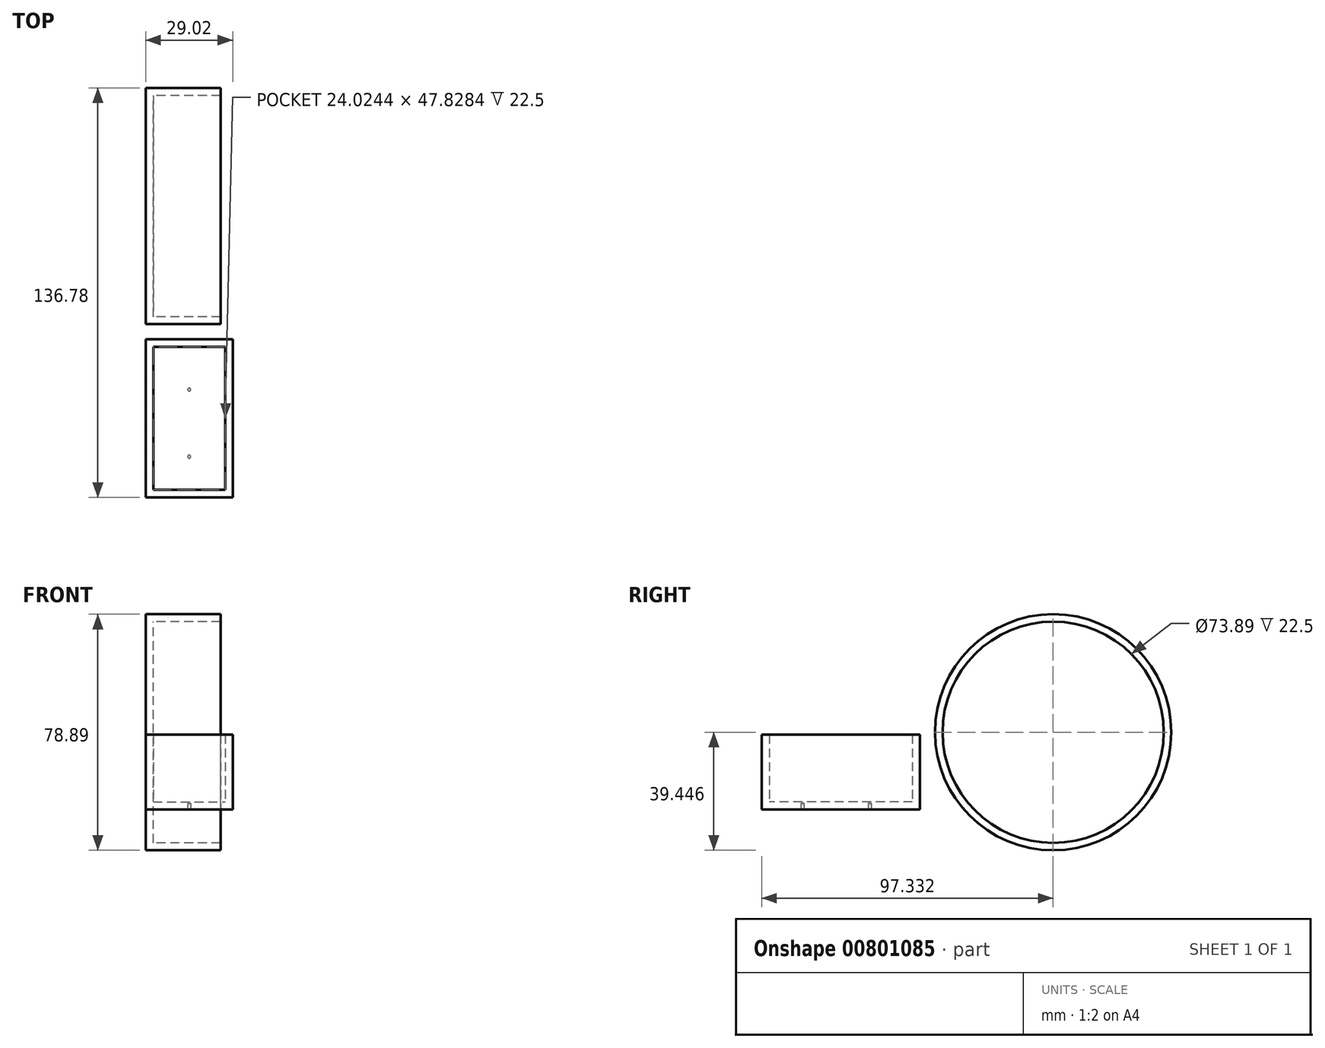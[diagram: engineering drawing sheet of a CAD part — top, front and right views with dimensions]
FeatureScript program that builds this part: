
annotation { "Feature Type Name" : "Feature", "Feature Type Description" : "" }
export const myFeature = defineFeature(function(context is Context, id is Id, definition is map)
    precondition{}
    {
        {
            var Q0;
            Q0=qCreatedBy(makeId("Top.planeOp"),FACE);
            var sketch = newSketch(context, id + "F0", { "sketchPlane" : qUnion([Q0])});
            skLineSegment(sketch, "E0.bottom", {"start": v(0, 0) * mm, "end": v(29.02, 0) * mm});
            skLineSegment(sketch, "E0.top", {"start": v(0, -52.83) * mm, "end": v(29.02, -52.83) * mm});
            skLineSegment(sketch, "E0.left", {"start": v(0, 0) * mm, "end": v(0, -52.83) * mm});
            skLineSegment(sketch, "E0.right", {"start": v(29.02, 0) * mm, "end": v(29.02, -52.83) * mm});
            skPoint(sketch, "E1", {"position": v(14.51, -39.21) * mm});
            skPoint(sketch, "E1.positionSnap0", {"position": v(14.51, -52.83) * mm});
            skPoint(sketch, "E2", {"position": v(14.51, -16.78) * mm});
            skSolve(sketch);
        }
        {
            var Q0;
            Q0 = qSketchRegion(id + "F0", true);
            extrude(context, id + "F1", {"entities" : qUnion([Q0]), "depth" : 25 * mm, "offsetDistance" : 25 * mm});
        }
        {
            var Q0;
            Q0=makeQuery(id+"F1.opExtrude","CAP_FACE",FACE,{"disambiguationData":[OSD([sQuery(id+"F0.wireOp",EDGE,"E0.bottom"),sQuery(id+"F0.wireOp",EDGE,"E0.top"),sQuery(id+"F0.wireOp",EDGE,"E0.left"),sQuery(id+"F0.wireOp",EDGE,"E0.right")])],"isStart":false});
            shell(context, id + "F2", {"entities" : qUnion([Q0]), "thickness" : 2.5 * mm});
        }
        {
            var Q0;
            Q0=sQuery(id+"F0.wireOp",VERTEX,"E2");
            var Q1;
            Q1=sQuery(id+"F0.wireOp",VERTEX,"E1");
            var Q2;
            Q2=makeQuery(id+"F1.opExtrude","SWEPT_BODY",BODY,{"disambiguationData":[OSD([sQuery(id+"F0.wireOp",EDGE,"E0.bottom"),sQuery(id+"F0.wireOp",EDGE,"E0.top"),sQuery(id+"F0.wireOp",EDGE,"E0.left"),sQuery(id+"F0.wireOp",EDGE,"E0.right")])]});
            hole(context, id + "F3", {"style" : HoleStyle.SIMPLE, "endStyle" : HoleEndStyle.BLIND, "oppositeDirection" : true, "holeDiameter" : 1 * mm, "majorDiameter" : 5 * mm, "holeDepth" : 2 * mm, "isTappedThrough" : true, "tappedDepth" : 12 * mm, "tapClearance" : 3, "startFromSketch" : true, "locations" : qUnion([Q0, Q1]), "scope" : qUnion([Q2])});
        }
        {
            var Q0;
            Q0=qCreatedBy(makeId("Right.planeOp"),FACE);
            var sketch = newSketch(context, id + "F4", { "sketchPlane" : qUnion([Q0])});
            skCircle(sketch, "E3", {"center": v(44.5, 25.83) * mm, "radius": 39.45 * mm});
            skSolve(sketch);
        }
        {
            var Q0;
            Q0=makeQuery(id+"F4.imprint","IMPRINT",FACE,{"disambiguationData":[TD([[makeQuery(id+"F4.imprint","IMPRINT",EDGE,{"derivedFrom":sQuery(id+"F4.wireOp",EDGE,"E3")}),1.0]])]});
            extrude(context, id + "F5", {"entities" : qUnion([Q0]), "depth" : 25 * mm, "offsetDistance" : 25 * mm});
        }
        {
            var Q0;
            Q0=makeQuery(id+"F5.opExtrude","CAP_FACE",FACE,{"disambiguationData":[OSD([sQuery(id+"F4.wireOp",EDGE,"E3")])],"isStart":false});
            shell(context, id + "F6", {"entities" : qUnion([Q0]), "thickness" : 2.5 * mm});
        }
    });
